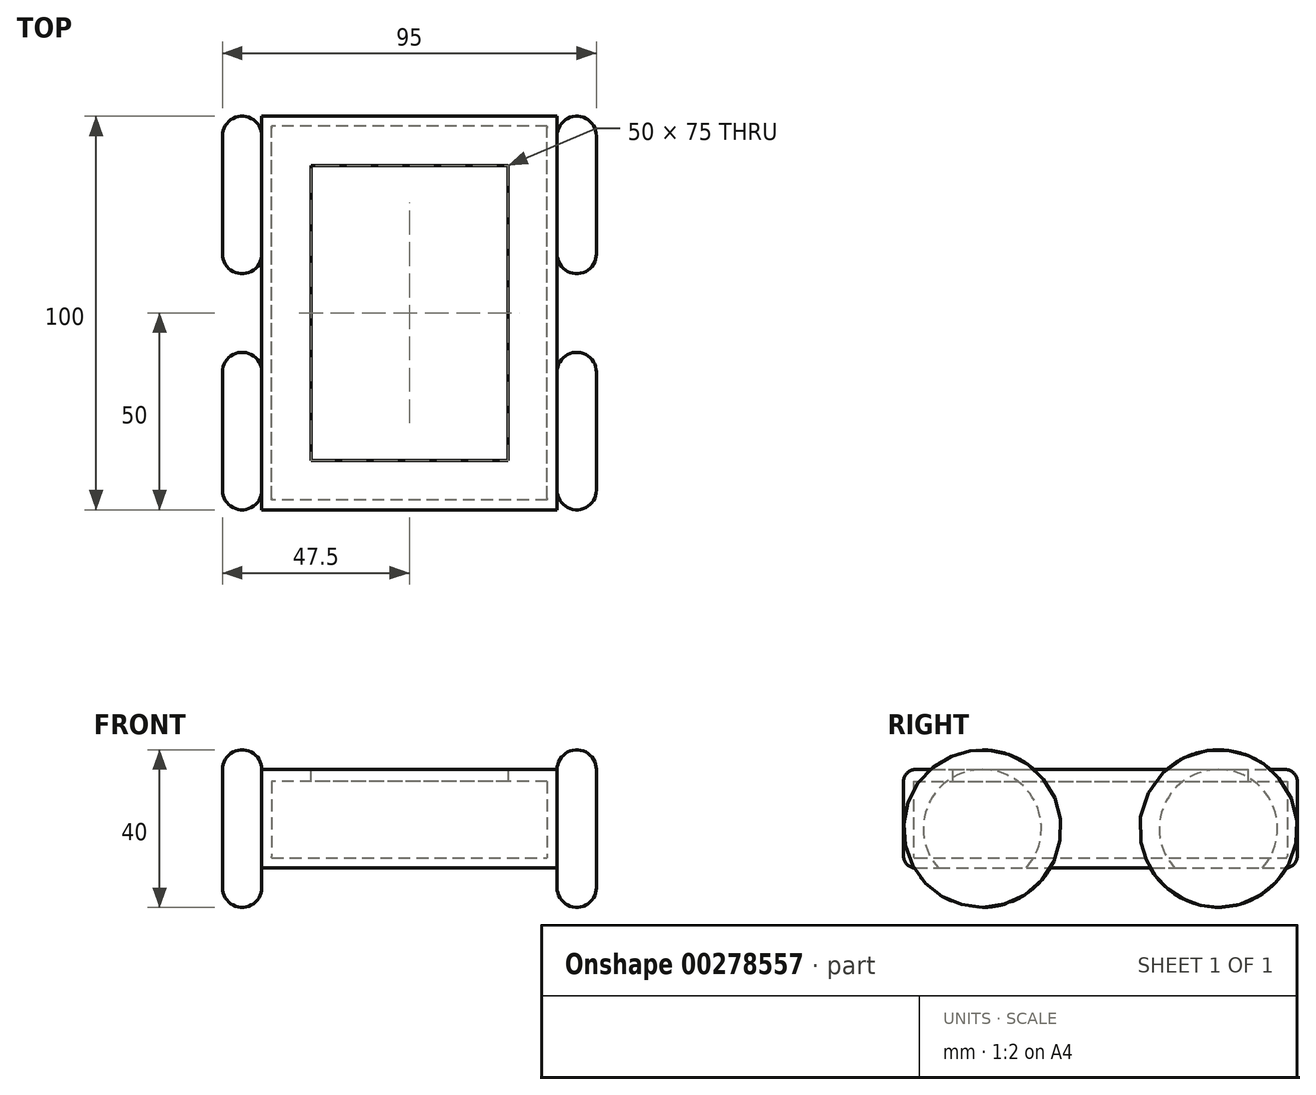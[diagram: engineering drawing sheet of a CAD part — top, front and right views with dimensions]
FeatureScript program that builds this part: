
annotation { "Feature Type Name" : "Feature", "Feature Type Description" : "" }
export const myFeature = defineFeature(function(context is Context, id is Id, definition is map)
    precondition{}
    {
        {
            var Q0;
            Q0=qCreatedBy(makeId("Top.planeOp"),FACE);
            var sketch = newSketch(context, id + "F0", { "sketchPlane" : qUnion([Q0])});
            skLineSegment(sketch, "E0.bottom", {"start": v(37.5, -50) * mm, "end": v(-37.5, -50) * mm});
            skLineSegment(sketch, "E0.top", {"start": v(37.5, 50) * mm, "end": v(-37.5, 50) * mm});
            skLineSegment(sketch, "E0.left", {"start": v(37.5, -50) * mm, "end": v(37.5, 50) * mm});
            skLineSegment(sketch, "E0.right", {"start": v(-37.5, -50) * mm, "end": v(-37.5, 50) * mm});
            skPoint(sketch, "E0.middle", {"position": v(0, 0) * mm});
            skSolve(sketch);
        }
        {
            var Q0;
            Q0=makeQuery(id+"F0.imprint","IMPRINT",FACE,{"disambiguationData":[TD([[makeQuery(id+"F0.imprint","IMPRINT",EDGE,{"derivedFrom":sQuery(id+"F0.wireOp",EDGE,"E0.bottom")}),-1.0]])]});
            extrude(context, id + "F1", {"entities" : qUnion([Q0]), "depth" : 10 * mm, "hasSecondDirection" : true, "secondDirectionOppositeDirection" : true, "secondDirectionDepth" : 10 * mm});
        }
        {
            var Q0;
            Q0=makeQuery(id+"F1.opExtrude","SWEPT_FACE",FACE,{"disambiguationData":[OSD([sQuery(id+"F0.wireOp",EDGE,"E0.right")])]});
            var sketch = newSketch(context, id + "F2", { "sketchPlane" : qUnion([Q0])});
            skLineSegment(sketch, "E1.0.0", {"start": v(-50, -10) * mm, "end": v(50, -10) * mm});
            skLineSegment(sketch, "E1.0.1", {"start": v(50, -10) * mm, "end": v(50, 10) * mm});
            skLineSegment(sketch, "E1.0.2", {"start": v(50, 10) * mm, "end": v(-50, 10) * mm});
            skLineSegment(sketch, "E1.0.3", {"start": v(-50, 10) * mm, "end": v(-50, -10) * mm});
            skLineSegment(sketch, "E2", {"start": v(-56.89, 0) * mm, "end": v(59.63, 0) * mm, "construction": true});
            skPoint(sketch, "E2.startSnap0", {"position": v(-50, 0) * mm});
            skPoint(sketch, "E2.endSnap0", {"position": v(50, 0) * mm});
            skCircle(sketch, "E3", {"center": v(-30, 0) * mm, "radius": 20 * mm});
            skCircle(sketch, "E4", {"center": v(30, 0) * mm, "radius": 20 * mm});
            skSolve(sketch);
        }
        {
            var Q0;
            {var subQ0=sQuery(id+"F2.wireOp",EDGE,"E3");var subQ1=sQuery(id+"F2.wireOp",EDGE,"E1.0.2");var subQ2=makeQuery(id+"F2.imprint","INTERSECT",VERTEX,{"disambiguationData":[OD(0.0)],"derivedFrom":[subQ1,subQ0]});Q0=makeQuery(id+"F2.imprint","IMPRINT",FACE,{"disambiguationData":[TD([[makeQuery(id+"F2.imprint","IMPRINT",EDGE,{"disambiguationData":[TD([[subQ2,-1.0]])],"derivedFrom":subQ1}),-1.0]])]});}
            var Q1;
            {var subQ0=sQuery(id+"F2.wireOp",EDGE,"E3");var subQ4=sQuery(id+"F2.wireOp",EDGE,"E1.0.0");var subQ7=makeQuery(id+"F2.imprint","INTERSECT",VERTEX,{"disambiguationData":[OD(0.0)],"derivedFrom":[subQ4,subQ0]});Q1=makeQuery(id+"F2.imprint","IMPRINT",FACE,{"disambiguationData":[TD([[makeQuery(id+"F2.imprint","IMPRINT",EDGE,{"disambiguationData":[TD([[subQ7,-1.0]])],"derivedFrom":subQ4}),-1.0]])]});}
            var Q2;
            {var subQ0=sQuery(id+"F2.wireOp",EDGE,"E3");var subQ1=sQuery(id+"F2.wireOp",EDGE,"E1.0.0");var subQ2=makeQuery(id+"F2.imprint","INTERSECT",VERTEX,{"disambiguationData":[OD(0.0)],"derivedFrom":[subQ1,subQ0]});Q2=makeQuery(id+"F2.imprint","IMPRINT",FACE,{"disambiguationData":[TD([[makeQuery(id+"F2.imprint","IMPRINT",EDGE,{"disambiguationData":[TD([[subQ2,-1.0]])],"derivedFrom":subQ1}),1.0]])]});}
            var Q3;
            {var subQ0=sQuery(id+"F2.wireOp",EDGE,"E4");var subQ1=sQuery(id+"F2.wireOp",EDGE,"E1.0.2");var subQ2=makeQuery(id+"F2.imprint","INTERSECT",VERTEX,{"disambiguationData":[OD(0.0)],"derivedFrom":[subQ1,subQ0]});Q3=makeQuery(id+"F2.imprint","IMPRINT",FACE,{"disambiguationData":[TD([[makeQuery(id+"F2.imprint","IMPRINT",EDGE,{"disambiguationData":[TD([[subQ2,-1.0]])],"derivedFrom":subQ1}),-1.0]])]});}
            var Q4;
            {var subQ0=sQuery(id+"F2.wireOp",EDGE,"E4");var subQ1=sQuery(id+"F2.wireOp",EDGE,"E1.0.0");var subQ7=makeQuery(id+"F2.imprint","INTERSECT",VERTEX,{"disambiguationData":[OD(0.0)],"derivedFrom":[subQ1,subQ0]});Q4=makeQuery(id+"F2.imprint","IMPRINT",FACE,{"disambiguationData":[TD([[makeQuery(id+"F2.imprint","IMPRINT",EDGE,{"disambiguationData":[TD([[subQ7,-1.0]])],"derivedFrom":subQ1}),-1.0]])]});}
            var Q5;
            {var subQ0=sQuery(id+"F2.wireOp",EDGE,"E4");var subQ1=sQuery(id+"F2.wireOp",EDGE,"E1.0.0");var subQ2=makeQuery(id+"F2.imprint","INTERSECT",VERTEX,{"disambiguationData":[OD(0.0)],"derivedFrom":[subQ1,subQ0]});Q5=makeQuery(id+"F2.imprint","IMPRINT",FACE,{"disambiguationData":[TD([[makeQuery(id+"F2.imprint","IMPRINT",EDGE,{"disambiguationData":[TD([[subQ2,-1.0]])],"derivedFrom":subQ1}),1.0]])]});}
            extrude(context, id + "F3", {"entities" : qUnion([Q0, Q1, Q2, Q3, Q4, Q5]), "depth" : 10 * mm});
        }
        {
            var Q0;
            Q0=makeQuery(id+"F3.opExtrude","SWEPT_BODY",BODY,{"disambiguationData":[OSD([sQuery(id+"F2.wireOp",EDGE,"E3")])]});
            var Q1;
            Q1=makeQuery(id+"F3.opExtrude","SWEPT_BODY",BODY,{"disambiguationData":[OSD([sQuery(id+"F2.wireOp",EDGE,"E4")])]});
            var Q2;
            Q2=qCreatedBy(makeId("Right.planeOp"),FACE);
            mirror(context, id + "F4", {"entities" : qUnion([Q0, Q1]), "mirrorPlane" : qUnion([Q2])});
        }
        {
            var Q0;
            Q0=makeQuery(id+"F1.opExtrude","CAP_EDGE",EDGE,{"disambiguationData":[OSD([sQuery(id+"F0.wireOp",EDGE,"E0.bottom")])],"isStart":true});
            var Q1;
            Q1=makeQuery(id+"F1.opExtrude","CAP_EDGE",EDGE,{"disambiguationData":[OSD([sQuery(id+"F0.wireOp",EDGE,"E0.top")])],"isStart":true});
            fillet(context, id + "F5", {"entities" : qUnion([Q0, Q1]), "radius" : 3 * mm, "tangentPropagation" : true, "allowEdgeOverflow" : false});
        }
        {
            var Q0;
            Q0=makeQuery(id+"F3.opExtrude","CAP_EDGE",EDGE,{"disambiguationData":[OSD([sQuery(id+"F2.wireOp",EDGE,"E4")])],"isStart":true});
            var Q1;
            Q1=makeQuery(id+"F3.opExtrude","CAP_EDGE",EDGE,{"disambiguationData":[OSD([sQuery(id+"F2.wireOp",EDGE,"E4")])],"isStart":false});
            var Q2;
            Q2=makeQuery(id+"F3.opExtrude","CAP_EDGE",EDGE,{"disambiguationData":[OSD([sQuery(id+"F2.wireOp",EDGE,"E3")])],"isStart":true});
            var Q3;
            Q3=makeQuery(id+"F3.opExtrude","CAP_EDGE",EDGE,{"disambiguationData":[OSD([sQuery(id+"F2.wireOp",EDGE,"E3")])],"isStart":false});
            var Q4;
            Q4=makeQuery(id+"F4.opPattern","COPY",EDGE,{"derivedFrom":makeQuery(id+"F3.opExtrude","CAP_EDGE",EDGE,{"disambiguationData":[OSD([sQuery(id+"F2.wireOp",EDGE,"E3")])],"isStart":true}),"instanceName":"1"});
            var Q5;
            Q5=makeQuery(id+"F4.opPattern","COPY",EDGE,{"derivedFrom":makeQuery(id+"F3.opExtrude","CAP_EDGE",EDGE,{"disambiguationData":[OSD([sQuery(id+"F2.wireOp",EDGE,"E3")])],"isStart":false}),"instanceName":"1"});
            var Q6;
            Q6=makeQuery(id+"F4.opPattern","COPY",EDGE,{"derivedFrom":makeQuery(id+"F3.opExtrude","CAP_EDGE",EDGE,{"disambiguationData":[OSD([sQuery(id+"F2.wireOp",EDGE,"E4")])],"isStart":false}),"instanceName":"1"});
            var Q7;
            Q7=makeQuery(id+"F4.opPattern","COPY",EDGE,{"derivedFrom":makeQuery(id+"F3.opExtrude","CAP_EDGE",EDGE,{"disambiguationData":[OSD([sQuery(id+"F2.wireOp",EDGE,"E4")])],"isStart":true}),"instanceName":"1"});
            fillet(context, id + "F6", {"entities" : qUnion([Q0, Q1, Q2, Q3, Q4, Q5, Q6, Q7]), "radius" : 5 * mm, "tangentPropagation" : true, "allowEdgeOverflow" : false});
        }
        {
            var Q0;
            Q0=makeQuery(id+"F1.opExtrude","CAP_FACE",FACE,{"disambiguationData":[OSD([sQuery(id+"F0.wireOp",EDGE,"E0.bottom"),sQuery(id+"F0.wireOp",EDGE,"E0.top"),sQuery(id+"F0.wireOp",EDGE,"E0.left"),sQuery(id+"F0.wireOp",EDGE,"E0.right")])],"isStart":false});
            shell(context, id + "F7", {"entities" : qUnion([Q0]), "thickness" : 2.5 * mm});
        }
        {
            var Q0;
            Q0=makeQuery(id+"F1.opExtrude","CAP_FACE",FACE,{"disambiguationData":[OSD([sQuery(id+"F0.wireOp",EDGE,"E0.bottom"),sQuery(id+"F0.wireOp",EDGE,"E0.top"),sQuery(id+"F0.wireOp",EDGE,"E0.left"),sQuery(id+"F0.wireOp",EDGE,"E0.right")])],"isStart":false});
            var sketch = newSketch(context, id + "F8", { "sketchPlane" : qUnion([Q0])});
            skLineSegment(sketch, "E5.0", {"start": v(-37.5, 50) * mm, "end": v(37.5, 50) * mm});
            skLineSegment(sketch, "E6.0", {"start": v(37.5, -50) * mm, "end": v(-37.5, -50) * mm});
            skLineSegment(sketch, "E7", {"start": v(-37.5, 50) * mm, "end": v(-37.5, -50) * mm});
            skLineSegment(sketch, "E8", {"start": v(37.5, 50) * mm, "end": v(37.5, -50) * mm});
            skSolve(sketch);
        }
        {
            var Q0;
            Q0=makeQuery(id+"F8.imprint","IMPRINT",FACE,{"disambiguationData":[TD([[makeQuery(id+"F8.imprint","IMPRINT",EDGE,{"derivedFrom":sQuery(id+"F8.wireOp",EDGE,"E5.0")}),1.0]])]});
            var sketch = newSketch(context, id + "F9", { "sketchPlane" : qUnion([Q0])});
            skLineSegment(sketch, "E9.0", {"start": v(37.5, -50) * mm, "end": v(-37.5, -50) * mm});
            skLineSegment(sketch, "E9.1", {"start": v(-37.5, 50) * mm, "end": v(-37.5, -50) * mm});
            skLineSegment(sketch, "E9.2", {"start": v(37.5, 50) * mm, "end": v(37.5, -50) * mm});
            skLineSegment(sketch, "E9.3", {"start": v(-37.5, 50) * mm, "end": v(37.5, 50) * mm});
            skLineSegment(sketch, "E10.0", {"start": v(-35, -47.5) * mm, "end": v(-35, 47.5) * mm});
            skLineSegment(sketch, "E10.1", {"start": v(35, 47.5) * mm, "end": v(-35, 47.5) * mm});
            skLineSegment(sketch, "E10.2", {"start": v(35, -47.5) * mm, "end": v(35, 47.5) * mm});
            skLineSegment(sketch, "E10.3", {"start": v(35, -47.5) * mm, "end": v(-35, -47.5) * mm});
            skSolve(sketch);
        }
        {
            var Q0;
            Q0 = qSketchRegion(id + "F9", true);
            extrude(context, id + "F10", {"entities" : qUnion([Q0]), "operationType" : NewBodyOperationType.ADD, "depth" : 5 * mm});
        }
        {
            var Q0;
            {var subQ0=sQuery(id+"F0.wireOp",EDGE,"E0.bottom");Q0=makeQuery(id+"F10.boolean.opBoolean","MERGE",FACE,{"derivedFrom":[makeQuery(id+"F7.opShell","OFFSET_FACE",FACE,{"disambiguationData":[OSD([subQ0]),TDD([makeQuery(id+"F1.opExtrude","SWEPT_FACE",FACE,{"disambiguationData":[OSD([subQ0])]})])]}),makeQuery(id+"F10.opExtrude","SWEPT_FACE",FACE,{"disambiguationData":[OSD([sQuery(id+"F9.wireOp",EDGE,"E10.3")])]})]});}
            var sketch = newSketch(context, id + "F11", { "sketchPlane" : qUnion([Q0])});
            skLineSegment(sketch, "E11.0.0", {"start": v(35, 12) * mm, "end": v(35, 15) * mm});
            skLineSegment(sketch, "E11.0.1", {"start": v(35, 15) * mm, "end": v(-35, 15) * mm});
            skLineSegment(sketch, "E11.0.2", {"start": v(-35, 15) * mm, "end": v(-35, 12) * mm});
            skLineSegment(sketch, "E11.0.3", {"start": v(-35, -7) * mm, "end": v(35, -7) * mm, "construction": true});
            skLineSegment(sketch, "E12", {"start": v(-35, 15) * mm, "end": v(-35, 12) * mm, "construction": true});
            skLineSegment(sketch, "E13", {"start": v(-35, 12) * mm, "end": v(35, 12) * mm});
            skLineSegment(sketch, "E14", {"start": v(35, 12) * mm, "end": v(35, 15) * mm, "construction": true});
            skLineSegment(sketch, "E15.2", {"start": v(-35, 15) * mm, "end": v(35, 15) * mm});
            skSolve(sketch);
        }
        {
            var Q0;
            Q0=makeQuery(id+"F10.boolean.opBoolean","MERGE",FACE,{"derivedFrom":[makeQuery(id+"F7.opShell","OFFSET_FACE",FACE,{"disambiguationData":[OSD([sQuery(id+"F0.wireOp",EDGE,"E0.left")])]}),makeQuery(id+"F10.opExtrude","SWEPT_FACE",FACE,{"disambiguationData":[OSD([sQuery(id+"F9.wireOp",EDGE,"E10.2")])]})]});
            var sketch = newSketch(context, id + "F12", { "sketchPlane" : qUnion([Q0])});
            skLineSegment(sketch, "E16.0", {"start": v(47.5, 15) * mm, "end": v(-47.5, 15) * mm});
            skLineSegment(sketch, "E17.0", {"start": v(-47.5, 15) * mm, "end": v(-47.5, -7) * mm});
            skLineSegment(sketch, "E18.0", {"start": v(47.5, 15) * mm, "end": v(47.5, -7) * mm});
            skLineSegment(sketch, "E19", {"start": v(47.5, 12) * mm, "end": v(-47.5, 12) * mm});
            skSolve(sketch);
        }
        {
            var Q0;
            {var subQ0=sQuery(id+"F0.wireOp",EDGE,"E0.top");Q0=makeQuery(id+"F10.boolean.opBoolean","MERGE",FACE,{"derivedFrom":[makeQuery(id+"F7.opShell","OFFSET_FACE",FACE,{"disambiguationData":[OSD([subQ0]),TDD([makeQuery(id+"F1.opExtrude","SWEPT_FACE",FACE,{"disambiguationData":[OSD([subQ0])]})])]}),makeQuery(id+"F10.opExtrude","SWEPT_FACE",FACE,{"disambiguationData":[OSD([sQuery(id+"F9.wireOp",EDGE,"E10.1")])]})]});}
            var sketch = newSketch(context, id + "F13", { "sketchPlane" : qUnion([Q0])});
            skLineSegment(sketch, "E20.0", {"start": v(35, 15) * mm, "end": v(-35, 15) * mm});
            skLineSegment(sketch, "E21.0", {"start": v(35, 15) * mm, "end": v(35, -7) * mm});
            skLineSegment(sketch, "E22.0", {"start": v(-35, 15) * mm, "end": v(-35, -7) * mm});
            skLineSegment(sketch, "E23", {"start": v(-35, 12) * mm, "end": v(35, 12) * mm});
            skSolve(sketch);
        }
        {
            var Q0;
            Q0=makeQuery(id+"F10.boolean.opBoolean","MERGE",FACE,{"derivedFrom":[makeQuery(id+"F7.opShell","OFFSET_FACE",FACE,{"disambiguationData":[OSD([sQuery(id+"F0.wireOp",EDGE,"E0.right")])]}),makeQuery(id+"F10.opExtrude","SWEPT_FACE",FACE,{"disambiguationData":[OSD([sQuery(id+"F9.wireOp",EDGE,"E10.0")])]})]});
            var sketch = newSketch(context, id + "F14", { "sketchPlane" : qUnion([Q0])});
            skLineSegment(sketch, "E24.0", {"start": v(-47.5, 15) * mm, "end": v(47.5, 15) * mm});
            skLineSegment(sketch, "E25.0", {"start": v(47.5, 15) * mm, "end": v(47.5, -7) * mm});
            skLineSegment(sketch, "E26.0", {"start": v(-47.5, 15) * mm, "end": v(-47.5, -7) * mm});
            skLineSegment(sketch, "E27", {"start": v(-47.5, 12) * mm, "end": v(47.5, 12) * mm});
            skSolve(sketch);
        }
        {
            var Q0;
            Q0 = qSketchRegion(id + "F14", true);
            extrude(context, id + "F15", {"entities" : qUnion([Q0]), "operationType" : NewBodyOperationType.ADD, "depth" : 10 * mm});
        }
        {
            var Q0;
            {var subQ0=sQuery(id+"F13.wireOp",EDGE,"E20.0");Q0=makeQuery(id+"F13.imprint","IMPRINT",FACE,{"disambiguationData":[TD([[makeQuery(id+"F13.imprint","IMPRINT",EDGE,{"derivedFrom":subQ0}),1.0]])]});}
            extrude(context, id + "F16", {"entities" : qUnion([Q0]), "operationType" : NewBodyOperationType.ADD, "depth" : 10 * mm});
        }
        {
            var Q0;
            {var subQ0=sQuery(id+"F12.wireOp",EDGE,"E16.0");Q0=makeQuery(id+"F12.imprint","IMPRINT",FACE,{"disambiguationData":[TD([[makeQuery(id+"F12.imprint","IMPRINT",EDGE,{"derivedFrom":subQ0}),1.0]])]});}
            extrude(context, id + "F17", {"entities" : qUnion([Q0]), "operationType" : NewBodyOperationType.ADD, "depth" : 10 * mm});
        }
        {
            var Q0;
            Q0=makeQuery(id+"F11.imprint","IMPRINT",FACE,{"disambiguationData":[TD([[makeQuery(id+"F11.imprint","IMPRINT",EDGE,{"derivedFrom":sQuery(id+"F11.wireOp",EDGE,"E11.0.0")}),-1.0]])]});
            extrude(context, id + "F18", {"entities" : qUnion([Q0]), "operationType" : NewBodyOperationType.ADD, "depth" : 10 * mm});
        }
        {
            var Q0;
            Q0=makeQuery(id+"F10.opExtrude","CAP_EDGE",EDGE,{"disambiguationData":[OSD([sQuery(id+"F9.wireOp",EDGE,"E9.3")])],"isStart":false});
            var Q1;
            Q1=makeQuery(id+"F10.opExtrude","CAP_EDGE",EDGE,{"disambiguationData":[OSD([sQuery(id+"F9.wireOp",EDGE,"E9.0")])],"isStart":false});
            fillet(context, id + "F19", {"entities" : qUnion([Q0, Q1]), "radius" : 3 * mm, "tangentPropagation" : true, "allowEdgeOverflow" : false});
        }
    });
